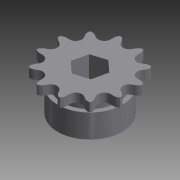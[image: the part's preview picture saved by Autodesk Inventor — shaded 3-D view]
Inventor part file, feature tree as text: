
AUTODESK INVENTOR PART (.ipt)
format: ipt  version: 2013 (Build 170138000, 138)  size: 259,584 bytes
history: native  units: mm (DEFAULTED — no unit token found)
features: extrude x2, sketch x2, imported_body x1
ambient origin geometry x8: Origin, YZ Plane, XZ Plane, XY Plane, X Axis, Y Axis, Z Axis, Center Point
bodies: Solid1 (feature_tree)
feature tree (5):
  imported_body  "Base1"
  extrude  "Extrusion1"  Depth=12.7mm
  extrude  "Extrusion2"  [1 undecoded]
  sketch  "Sketch1"  dims[d0=19.2532mm d1=0.0mm d2=12.7mm]
  sketch  "Sketch2"  dims[d3=19.2532mm d4=0.0mm]
note: 1 required parameter value undecoded (feature->parameter linkage not recoverable at this tier; creation-order binding heuristic only, values carry confidence <= 0.55)
